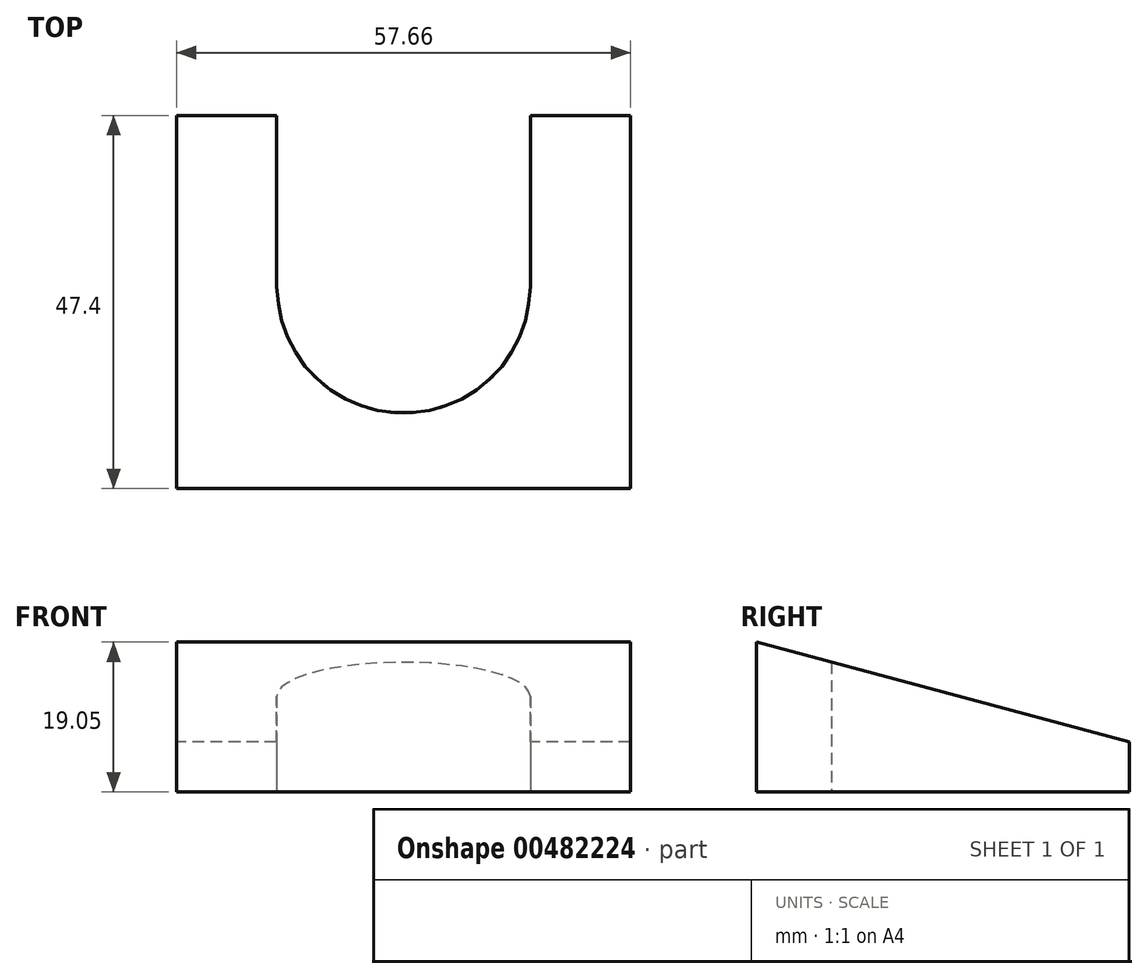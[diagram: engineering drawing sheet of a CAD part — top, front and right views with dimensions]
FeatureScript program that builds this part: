
annotation { "Feature Type Name" : "Feature", "Feature Type Description" : "" }
export const myFeature = defineFeature(function(context is Context, id is Id, definition is map)
    precondition{}
    {
        {
            var Q0;
            Q0=qCreatedBy(makeId("Right.planeOp"),FACE);
            var sketch = newSketch(context, id + "F0", { "sketchPlane" : qUnion([Q0])});
            skLineSegment(sketch, "E0", {"start": v(0, 0) * mm, "end": v(0, 6.35) * mm});
            skLineSegment(sketch, "E1", {"start": v(0, 6.35) * mm, "end": v(-47.4, 19.05) * mm});
            skLineSegment(sketch, "E2", {"start": v(-47.4, 19.05) * mm, "end": v(-47.4, 0) * mm});
            skLineSegment(sketch, "E3", {"start": v(-47.4, 0) * mm, "end": v(0, 0) * mm});
            skSolve(sketch);
        }
        {
            var Q0;
            Q0 = qSketchRegion(id + "F0", true);
            extrude(context, id + "F1", {"entities" : qUnion([Q0]), "depth" : 57.66 * mm});
        }
        {
            var Q0;
            Q0=makeQuery(id+"F1.opExtrude","SWEPT_FACE",FACE,{"disambiguationData":[OSD([sQuery(id+"F0.wireOp",EDGE,"E3")])]});
            var sketch = newSketch(context, id + "F2", { "sketchPlane" : qUnion([Q0])});
            skPoint(sketch, "E4", {"position": v(12.7, 0) * mm});
            skLineSegment(sketch, "E5.bottom", {"start": v(12.7, 0) * mm, "end": v(44.96, 0) * mm});
            skLineSegment(sketch, "E5.left", {"start": v(12.7, 0) * mm, "end": v(12.7, 21.74) * mm});
            skLineSegment(sketch, "E5.right", {"start": v(44.96, 0) * mm, "end": v(44.96, 21.74) * mm});
            skArc(sketch, "E6", {"start": v(44.96, 21.74) * mm, "mid": v(28.83, 37.87) * mm, "end": v(12.7, 21.74) * mm});
            skSolve(sketch);
        }
        {
            var Q0;
            Q0 = qSketchRegion(id + "F2", true);
            extrude(context, id + "F3", {"entities" : qUnion([Q0]), "operationType" : NewBodyOperationType.REMOVE, "flatOperationType" : FlatOperationType.REMOVE, "endBound" : BoundingType.THROUGH_ALL, "oppositeDirection" : true, "offsetDistance" : 25.4 * mm, "depth" : 25.4 * mm, "domain" : OperationDomain.MODEL});
        }
    });
